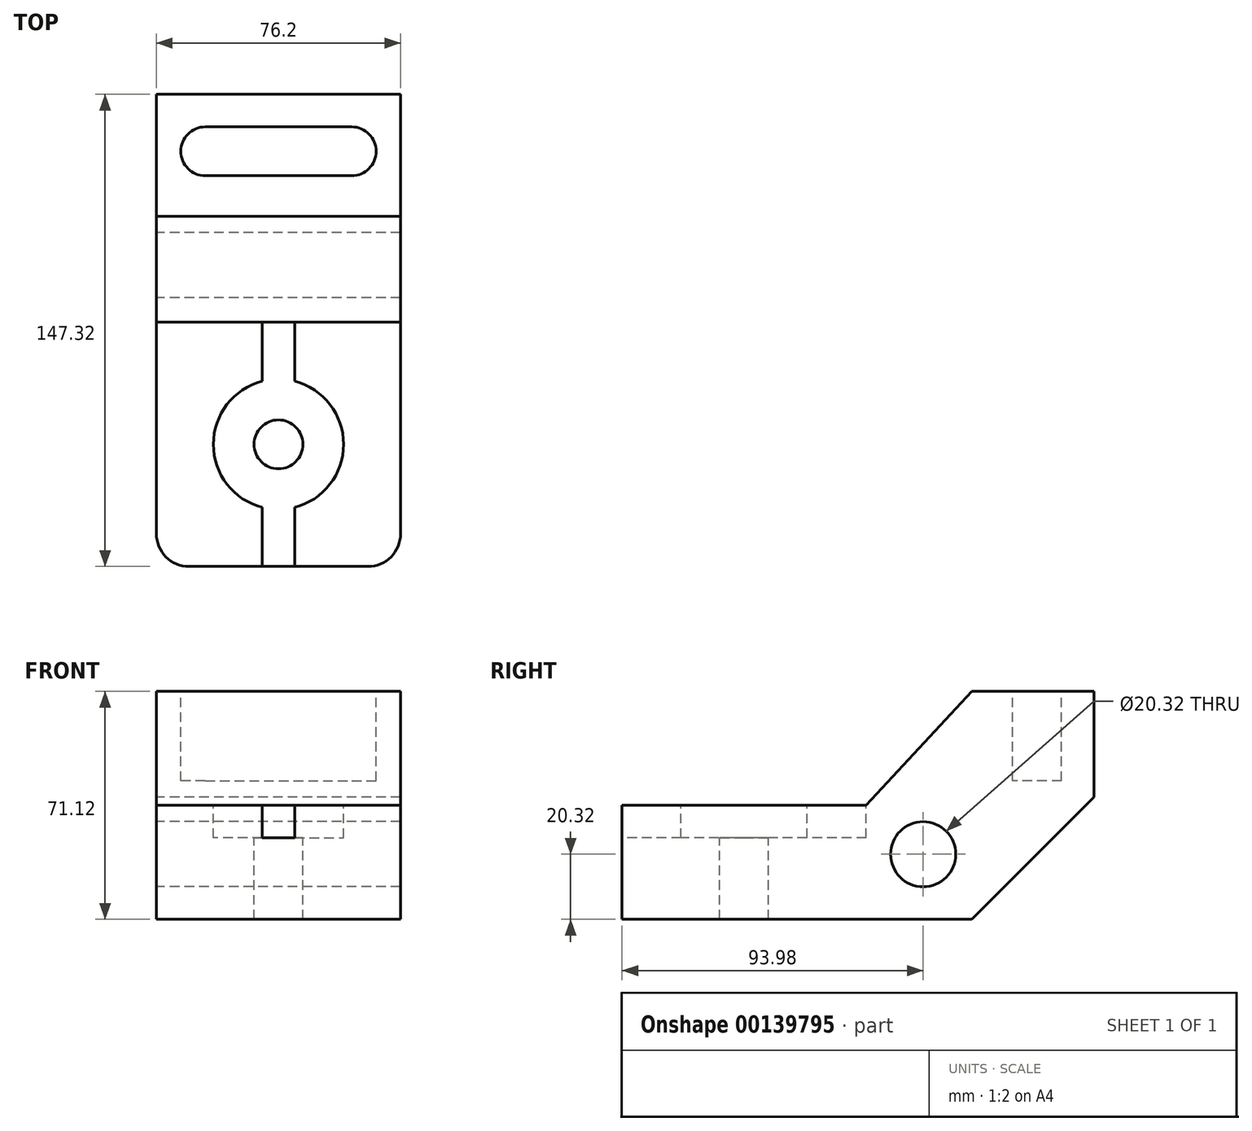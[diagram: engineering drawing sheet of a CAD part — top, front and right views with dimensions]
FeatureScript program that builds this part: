
annotation { "Feature Type Name" : "Feature", "Feature Type Description" : "" }
export const myFeature = defineFeature(function(context is Context, id is Id, definition is map)
    precondition{}
    {
        {
            var Q0;
            Q0=qCreatedBy(makeId("Right.planeOp"),FACE);
            var sketch = newSketch(context, id + "F0", { "sketchPlane" : qUnion([Q0])});
            skLineSegment(sketch, "E0", {"start": v(0, 0) * mm, "end": v(-109.22, 0) * mm});
            skLineSegment(sketch, "E1", {"start": v(-109.22, 0) * mm, "end": v(-109.22, 35.56) * mm});
            skLineSegment(sketch, "E2", {"start": v(-109.22, 35.56) * mm, "end": v(-33.02, 35.56) * mm});
            skLineSegment(sketch, "E3", {"start": v(-33.02, 35.56) * mm, "end": v(0, 71.12) * mm});
            skLineSegment(sketch, "E4", {"start": v(0, 71.12) * mm, "end": v(38.1, 71.12) * mm});
            skLineSegment(sketch, "E5", {"start": v(38.1, 71.12) * mm, "end": v(38.1, 38.1) * mm});
            skLineSegment(sketch, "E6", {"start": v(38.1, 38.1) * mm, "end": v(0, 0) * mm});
            skCircle(sketch, "E7", {"center": v(-15.24, 20.32) * mm, "radius": 10.16 * mm});
            skSolve(sketch);
        }
        {
            var Q0;
            Q0 = qSketchRegion(id + "F0", true);
            extrude(context, id + "F1", {"entities" : qUnion([Q0]), "endBound" : BoundingType.SYMMETRIC, "depth" : 76.2 * mm});
        }
        {
            var Q0;
            Q0=makeQuery(id+"F1.opExtrude","SWEPT_FACE",FACE,{"disambiguationData":[OSD([sQuery(id+"F0.wireOp",EDGE,"E4")])]});
            var sketch = newSketch(context, id + "F2", { "sketchPlane" : qUnion([Q0])});
            skArc(sketch, "E8", {"start": v(-22.86, 27.94) * mm, "mid": v(-30.48, 20.32) * mm, "end": v(-22.86, 12.7) * mm});
            skArc(sketch, "E9", {"start": v(22.86, 12.7) * mm, "mid": v(30.48, 20.32) * mm, "end": v(22.86, 27.94) * mm});
            skLineSegment(sketch, "E10", {"start": v(-22.86, 27.94) * mm, "end": v(22.86, 27.94) * mm});
            skLineSegment(sketch, "E11", {"start": v(-22.86, 12.7) * mm, "end": v(22.86, 12.7) * mm});
            skSolve(sketch);
        }
        {
            var Q0;
            Q0 = qSketchRegion(id + "F2", true);
            extrude(context, id + "F3", {"entities" : qUnion([Q0]), "operationType" : NewBodyOperationType.REMOVE, "oppositeDirection" : true, "depth" : 27.94 * mm});
        }
        {
            var Q0;
            Q0=makeQuery(id+"F1.opExtrude","SWEPT_FACE",FACE,{"disambiguationData":[OSD([sQuery(id+"F0.wireOp",EDGE,"E1")])]});
            var sketch = newSketch(context, id + "F4", { "sketchPlane" : qUnion([Q0])});
            skLineSegment(sketch, "E12.bottom", {"start": v(-5.08, 25.4) * mm, "end": v(5.08, 25.4) * mm});
            skLineSegment(sketch, "E12.left", {"start": v(-5.08, 25.4) * mm, "end": v(-5.08, 35.56) * mm});
            skLineSegment(sketch, "E12.right", {"start": v(5.08, 25.4) * mm, "end": v(5.08, 35.56) * mm});
            skPoint(sketch, "E12.middle", {"position": v(0, 35.56) * mm});
            skPoint(sketch, "E13", {"position": v(-5.08, 35.56) * mm});
            skPoint(sketch, "E14", {"position": v(5.08, 35.56) * mm});
            skLineSegment(sketch, "E15", {"start": v(-5.08, 35.56) * mm, "end": v(5.08, 35.56) * mm});
            skLineSegment(sketch, "E16.0", {"start": v(38.1, 35.56) * mm, "end": v(-38.1, 35.56) * mm});
            skSolve(sketch);
        }
        {
            var Q0;
            Q0=makeQuery(id+"F1.opExtrude","SWEPT_FACE",FACE,{"disambiguationData":[OSD([sQuery(id+"F0.wireOp",EDGE,"E2")])]});
            var sketch = newSketch(context, id + "F5", { "sketchPlane" : qUnion([Q0])});
            skPoint(sketch, "E17", {"position": v(0, -71.12) * mm});
            skSolve(sketch);
        }
        {
            var Q0;
            Q0=sQuery(id+"F5.wireOp",VERTEX,"E17");
            var Q1;
            Q1=makeQuery(id+"F1.opExtrude","SWEPT_BODY",BODY,{"disambiguationData":[OSD([sQuery(id+"F0.wireOp",EDGE,"E0"),sQuery(id+"F0.wireOp",EDGE,"E1"),sQuery(id+"F0.wireOp",EDGE,"E2"),sQuery(id+"F0.wireOp",EDGE,"E3"),sQuery(id+"F0.wireOp",EDGE,"E4"),sQuery(id+"F0.wireOp",EDGE,"E5"),sQuery(id+"F0.wireOp",EDGE,"E6"),sQuery(id+"F0.wireOp",EDGE,"E7")])]});
            hole(context, id + "F6", {"style" : HoleStyle.C_BORE, "endStyle" : HoleEndStyle.THROUGH, "holeDiameter" : 15.24 * mm, "cBoreDiameter" : 40.64 * mm, "cBoreDepth" : 10.16 * mm, "locations" : qUnion([Q0]), "scope" : qUnion([Q1]), "isTappedThrough" : true});
        }
        {
            var Q0;
            Q0 = qSketchRegion(id + "F4", true);
            extrude(context, id + "F7", {"entities" : qUnion([Q0]), "operationType" : NewBodyOperationType.REMOVE, "oppositeDirection" : true, "depth" : 76.2 * mm});
        }
        {
            var Q0;
            Q0=makeQuery(id+"F1.opExtrude","CAP_EDGE",EDGE,{"disambiguationData":[OSD([sQuery(id+"F0.wireOp",EDGE,"E1")])],"isStart":true});
            var Q1;
            Q1=makeQuery(id+"F1.opExtrude","CAP_EDGE",EDGE,{"disambiguationData":[OSD([sQuery(id+"F0.wireOp",EDGE,"E1")])],"isStart":false});
            fillet(context, id + "F8", {"entities" : qUnion([Q0, Q1]), "radius" : 10.16 * mm, "tangentPropagation" : true, "allowEdgeOverflow" : false});
        }
    });
